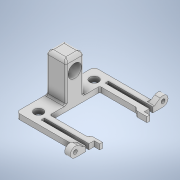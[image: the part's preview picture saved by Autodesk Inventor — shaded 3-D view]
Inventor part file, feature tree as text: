
AUTODESK INVENTOR PART (.ipt)
format: ipt  version: 2020 (Build 240168000, 168)  size: 325,632 bytes
history: native  units: in
note: dims shown in document units (in); Inventor stores cm internally (conversion verified against a paired STEP export)
features: extrude x7, sketch x5, fillet x4
ambient origin geometry x8: Origin, YZ Plane, XZ Plane, XY Plane, X Axis, Y Axis, Z Axis, Center Point
bodies: Solid1 (feature_tree)
feature tree (16):
  extrude  "Extrusion1"  Depth=2.2638in
  extrude  "Extrusion5"  Depth=0.315in
  extrude  "Extrusion6"  Depth=0.3937in
  fillet  "Fillet6"  Radius=0.8858in
  extrude  "Extrusion7"  Depth=0.0591in
  extrude  "Extrusion8"  Depth=0.1181in
  fillet  "Fillet7"  [1 undecoded]
  extrude  "Extrusion9"  Depth=0.1181in
  fillet  "Fillet9"  Radius=0.9843in
  extrude  "Extrusion11"  Depth=0.3543in
  fillet  "Fillet10"  Radius=0.1378in
  sketch  "Sketch5"  dims[d0=2.7559in d1=2.2638in]
  sketch  "Sketch6"  dims[d2=0.1875in d3=0.0in d4=0.315in]
  sketch  "Sketch7"  dims[d5=0.3937in d6=0.3937in d7=0.8858in]
  sketch  "Sketch8"  dims[d8=1.5748in d9=0.0591in]
  sketch  "Sketch11"  dims[d10=1.5748in d11=0.1181in d45=0.0in d46=0.1181in d47=0.9843in d48=0.0in d49=0.3543in d50=0.1378in d51=0.1969in d52=0.0in d59=0.0625in d60=0.3937in d61=0.0984in d62=0.0in d63=0.3937in d64=0.0984in d65=0.0in d66=0.125in d71=1.378in d72=0.0in d79=0.1378in d80=0.1378in d87=0.0591in d88=0.6299in d89=1.063in d90=0.4724in d91=1.1024in d92=1.378in d93=0.0in d94=0.125in]
note: 1 required parameter value undecoded (feature->parameter linkage not recoverable at this tier; creation-order binding heuristic only, values carry confidence <= 0.55)
